# Revit family: Storage-Teknion-CTCE_Double_Combination_Tower_Elevated-R2021
name_source: partatom
category: Furniture
units: mm (PartAtom-declared; Revit-internal decimal feet)

## family parameters
Always vertical = Yes
Cut with Voids When Loaded = No
OmniClass Number = 23.40.20.00
OmniClass Title = General Furniture and Specialties
Room Calculation Point = No
Shared = Yes
Work Plane-Based = No

## types (8) — shared parameters
Assembly Code = E2020200
Height Option = Select Height Option. 5E - 5 High Elevated (70.25 Inch) are default.
Manufacturer = Teknion
Manufacturer Fax = 416.661.4586
Part Number = CTCE
Product Documentation Link = https://www.teknion.com
Product Line = Bookcases, Stackers & Towers
Product Page URL = https://www.teknion.com
Series = Chronicle
Shelf 2 = Yes
Shelf 3 = Yes
Shelf 4 = Yes
Shelf 5/Top 5E = Yes
Sustainability Data = https://www.teknion.com
URL = www.teknion.com
Unit Weight URL = http://www.teknion.com
Warranty = http://www.teknion.com
zero-valued in all types: Default Elevation

## per-type parameters (varying)
| type | 5E - 5 High Elevated (70.25" Height) | 6E - 6 High Elevated (84" Height) | Cut-Out - Front - Horizontal | Cut-Out - Front - Vertical | Description | Drawer | Front - Upper | HH - Hinged Doors Upper, Hinged Doors Lower | HX - Hinged Doors Upper, 1 Box 1 File Lower | MR - Front | MR - Front - Hinged Doors | Model | OH - Open Upper, Hinged Doors Lower | OX - Open Upper, 1 Box 1 File Lower | Shelf 1 | Shelf 5/Top 6E - Back Distance | Shelf 5/Top 6E - Front Distance | Top - 6E |
| Open Upper, 1 Box 1 File Lower (OX), 5 High Elevated (70.25" Height) | Yes | No | 3 " | 0.5 " | Double Combination Tower, Elevated, Open Upper, 1 Box 1 File Lower Configuration, 5 High Elevated (70.25" Height) | Yes | No | No | No | Yes | No | CTCEOX5E____ | No | Yes | No | 0 " | 0.843 " | No |
| Open Upper, Hinged Doors Lower (OH), 5 High Elevated (70.25" Height) | Yes | No | 0.5 " | 3 " | Double Combination Tower, Elevated, Open Upper, Hinged Doors Lower Configuration, 5 High Elevated (70.25" Height) | No | No | No | No | No | Yes | CTCEOH5E____ | Yes | No | Yes | 0 " | 0.843 " | No |
| Hinged Doors Upper, 1 Box 1 File Lower (HX), 5 High Elevated (70.25" Height) | Yes | No | 3 " | 0.5 " | Double Combination Tower, Elevated, Hinged Doors Upper, 1 Box 1 File Lower Configuration, 5 High Elevated (70.25" Height), None Shelf Edge Profile | Yes | Yes | No | Yes | Yes | No | CTCEHX5E__N_ | No | No | No | 0 " | 0.843 " | No |
| Hinged Doors Upper, Hinged Doors Lower (HH), 5 High Elevated (70.25" Height) | Yes | No | 0.5 " | 3 " | Double Combination Tower, Elevated, Hinged Doors Upper, Hinged Doors Lower Configuration, 5 High Elevated (70.25" Height), None Shelf Edge Profile | No | Yes | Yes | No | No | Yes | CTCEHH5E__N_ | No | No | Yes | 0 " | 0.843 " | No |
| Hinged Doors Upper, 1 Box 1 File Lower (HX), 6 High Elevated (84" Height) | No | Yes | 3 " | 0.5 " | Double Combination Tower, Elevated, Hinged Doors Upper, 1 Box 1 File Lower Configuration, 6 High Elevated (84" Height), None Shelf Edge Profile | Yes | Yes | No | Yes | Yes | No | CTCEHX6E__N_ | No | No | No | 1.474 " | 1.843 " | Yes |
| Hinged Doors Upper, Hinged Doors Lower (HH), 6 High Elevated (84" Height) | No | Yes | 0.5 " | 3 " | Double Combination Tower, Elevated, Hinged Doors Upper, Hinged Doors Lower Configuration, 6 High Elevated (84" Height), None Shelf Edge Profile | No | Yes | Yes | No | No | Yes | CTCEHH6E__N_ | No | No | Yes | 1.474 " | 1.843 " | Yes |
| Open Upper, 1 Box 1 File Lower (OX), 6 High Elevated (84" Height) | No | Yes | 3 " | 0.5 " | Double Combination Tower, Elevated, Open Upper, 1 Box 1 File Lower Configuration, 6 High Elevated (84" Height) | Yes | No | No | No | Yes | No | CTCEOX6E____ | No | Yes | No | 1.474 " | 1.843 " | Yes |
| Open Upper, Hinged Doors Lower (OH), 6 High Elevated (84" Height) | No | Yes | 0.5 " | 3 " | Double Combination Tower, Elevated, Open Upper, Hinged Doors Lower Configuration, 6 High Elevated (84" Height) | No | No | No | No | No | Yes | CTCEOH6E____ | Yes | No | Yes | 1.474 " | 1.843 " | Yes |

## geometry (parser evidence)
native form markers: Sweep x2
no freeform markers — native parametric forms only
